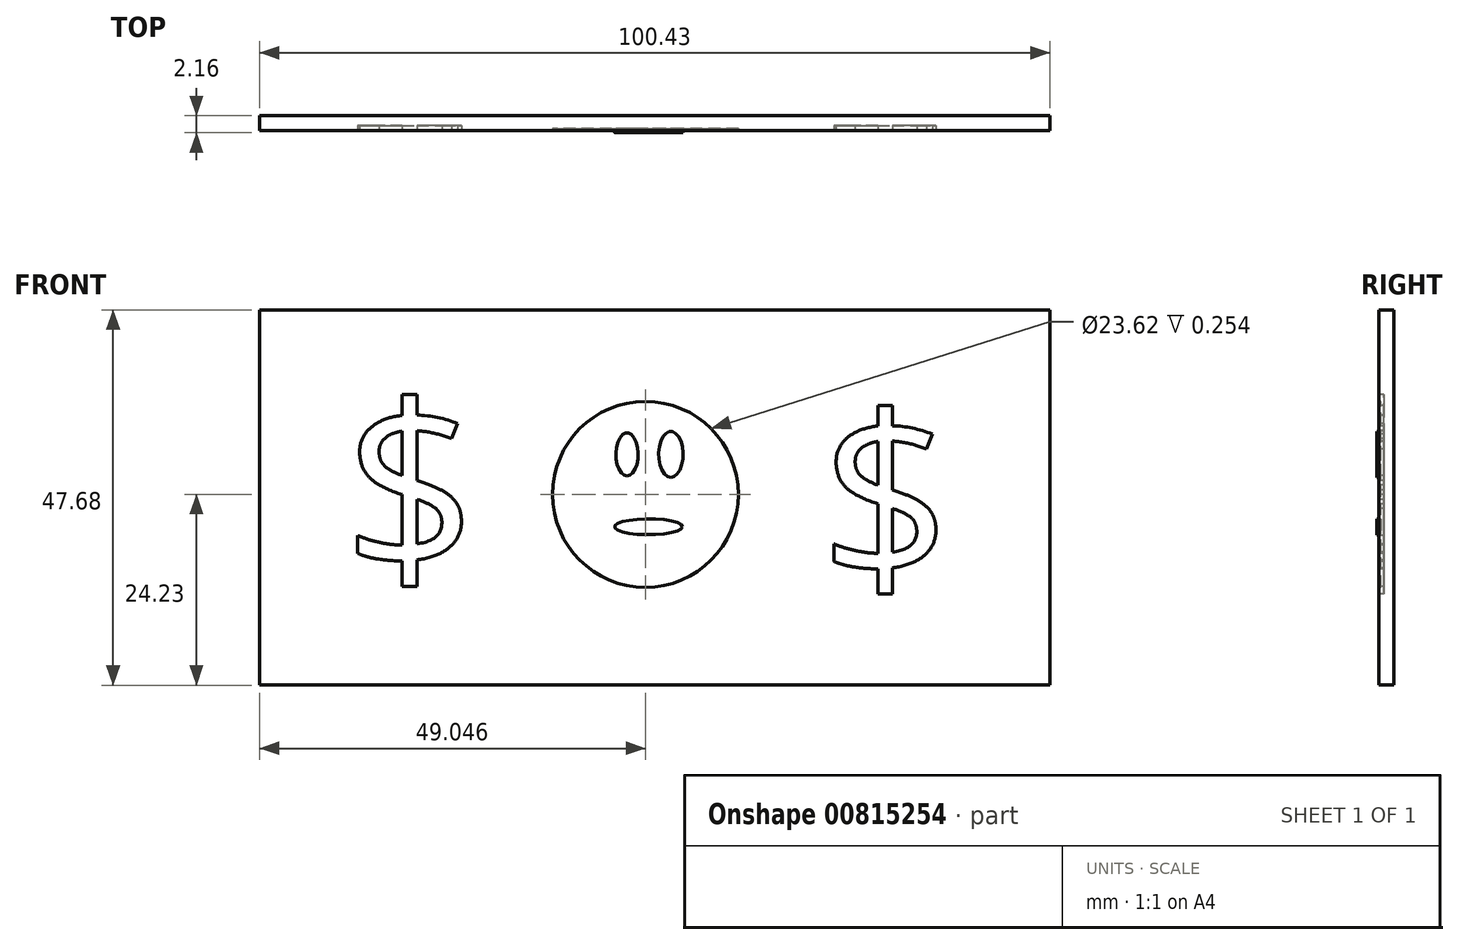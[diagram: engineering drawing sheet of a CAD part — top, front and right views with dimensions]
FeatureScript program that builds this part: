
annotation { "Feature Type Name" : "Feature", "Feature Type Description" : "" }
export const myFeature = defineFeature(function(context is Context, id is Id, definition is map)
    precondition{}
    {
        {
            var Q0;
            Q0=qCreatedBy(makeId("Front.planeOp"),FACE);
            var sketch = newSketch(context, id + "F0", { "sketchPlane" : qUnion([Q0])});
            skLineSegment(sketch, "E0.bottom", {"start": v(-52.27, 23.45) * mm, "end": v(48.16, 23.45) * mm});
            skLineSegment(sketch, "E0.top", {"start": v(-52.27, -24.23) * mm, "end": v(48.16, -24.23) * mm});
            skLineSegment(sketch, "E0.left", {"start": v(-52.27, 23.45) * mm, "end": v(-52.27, -24.23) * mm});
            skLineSegment(sketch, "E0.right", {"start": v(48.16, 23.45) * mm, "end": v(48.16, -24.23) * mm});
            skSolve(sketch);
        }
        {
            var Q0;
            Q0=makeQuery(id+"F0.imprint","IMPRINT",FACE,{"disambiguationData":[TD([[makeQuery(id+"F0.imprint","IMPRINT",EDGE,{"derivedFrom":sQuery(id+"F0.wireOp",EDGE,"E0.bottom")}),-1.0]])]});
            extrude(context, id + "F1", {"entities" : qUnion([Q0]), "depth" : 1.9 * mm, "offsetDistance" : 25.4 * mm});
        }
        {
            var Q0;
            Q0=makeQuery(id+"F1.opExtrude","CAP_FACE",FACE,{"disambiguationData":[OSD([sQuery(id+"F0.wireOp",EDGE,"E0.bottom"),sQuery(id+"F0.wireOp",EDGE,"E0.top"),sQuery(id+"F0.wireOp",EDGE,"E0.left"),sQuery(id+"F0.wireOp",EDGE,"E0.right")])],"isStart":false});
            var sketch = newSketch(context, id + "F2", { "sketchPlane" : qUnion([Q0])});
            skText(sketch, "E1", { "text": "$", "fontName": "OpenSans-Regular.ttf"});
            const initialGuessF2  = {"E1": [-0.04171, -0.00996, 1, 0, 0.0215]};
            skSetInitialGuess(sketch, initialGuessF2);
            skSolve(sketch);
        }
        {
            var Q0;
            Q0=makeQuery(id+"F2.imprint","IMPRINT",FACE,{"disambiguationData":[TD([[makeQuery(id+"F2.imprint","IMPRINT",EDGE,{"derivedFrom":sQuery(id+"F2.wireOp",EDGE,"E1.sketch_text.stroke-0")}),1.0]])]});
            var sketch = newSketch(context, id + "F3", { "sketchPlane" : qUnion([Q0])});
            skText(sketch, "E2", { "text": "$", "fontName": "OpenSans-Regular.ttf"});
            const initialGuessF3  = {"E2": [0.01885, -0.01094, 1, 0, 0.0211]};
            skSetInitialGuess(sketch, initialGuessF3);
            skSolve(sketch);
        }
        {
            var Q0;
            Q0 = qSketchRegion(id + "F2", true);
            var Q1;
            Q1 = qSketchRegion(id + "F3", true);
            extrude(context, id + "F4", {"entities" : qUnion([Q0, Q1]), "operationType" : NewBodyOperationType.REMOVE, "oppositeDirection" : true, "depth" : 0.64 * mm, "offsetDistance" : 25.4 * mm});
        }
        {
            var Q0;
            {var subQ0=sQuery(id+"F0.wireOp",EDGE,"E0.right");var subQ1=sQuery(id+"F0.wireOp",EDGE,"E0.left");var subQ2=sQuery(id+"F0.wireOp",EDGE,"E0.bottom");var subQ3=sQuery(id+"F0.wireOp",EDGE,"E0.top");Q0=makeQuery(id+"F4.boolean.opBoolean","SPLIT",FACE,{"disambiguationData":[TD([makeQuery(id+"F1.opExtrude","SWEPT_FACE",FACE,{"disambiguationData":[OSD([subQ2])]})])],"derivedFrom":makeQuery(id+"F1.opExtrude","CAP_FACE",FACE,{"disambiguationData":[OSD([subQ2,subQ3,subQ1,subQ0])],"isStart":false})});}
            var sketch = newSketch(context, id + "F5", { "sketchPlane" : qUnion([Q0])});
            skCircle(sketch, "E3", {"center": v(-3.22, 0) * mm, "radius": 11.8 * mm});
            skSolve(sketch);
        }
        {
            var Q0;
            Q0=makeQuery(id+"F5.imprint","IMPRINT",FACE,{"disambiguationData":[TD([[makeQuery(id+"F5.imprint","IMPRINT",EDGE,{"derivedFrom":sQuery(id+"F5.wireOp",EDGE,"E3")}),1.0]])]});
            extrude(context, id + "F6", {"entities" : qUnion([Q0]), "operationType" : NewBodyOperationType.REMOVE, "oppositeDirection" : true, "depth" : 0.25 * mm, "offsetDistance" : 25.4 * mm});
        }
        {
            var Q0;
            Q0=makeQuery(id+"F6.boolean.opBoolean","COPY",FACE,{"derivedFrom":makeQuery(id+"F6.opExtrude","CAP_FACE",FACE,{"disambiguationData":[OSD([sQuery(id+"F5.wireOp",EDGE,"E3")])],"isStart":false})});
            var sketch = newSketch(context, id + "F7", { "sketchPlane" : qUnion([Q0])});
            skEllipse(sketch, "E4", {"center": v(-5.57, 5.08) * mm, "majorRadius": 2.74 * mm, "minorRadius": 1.4 * mm, "majorAxis": v(0, -1)});
            skEllipse(sketch, "E5", {"center": v(0, 5.08) * mm, "majorRadius": 2.93 * mm, "minorRadius": 1.55 * mm, "majorAxis": v(0, -1)});
            skPoint(sketch, "E5.centerSnap0", {"position": v(-4.17, 5.08) * mm});
            skEllipse(sketch, "E6", {"center": v(-2.83, -4.1) * mm, "majorRadius": 4.3 * mm, "minorRadius": 1.01 * mm, "majorAxis": v(1, 0)});
            skSolve(sketch);
        }
        {
            var Q0;
            Q0=makeQuery(id+"F7.imprint","IMPRINT",FACE,{"disambiguationData":[TD([[makeQuery(id+"F7.imprint","IMPRINT",EDGE,{"derivedFrom":sQuery(id+"F7.wireOp",EDGE,"E4")}),1.0]])]});
            var Q1;
            Q1=makeQuery(id+"F7.imprint","IMPRINT",FACE,{"disambiguationData":[TD([[makeQuery(id+"F7.imprint","IMPRINT",EDGE,{"derivedFrom":sQuery(id+"F7.wireOp",EDGE,"E5")}),1.0]])]});
            var Q2;
            Q2=makeQuery(id+"F7.imprint","IMPRINT",FACE,{"disambiguationData":[TD([[makeQuery(id+"F7.imprint","IMPRINT",EDGE,{"derivedFrom":sQuery(id+"F7.wireOp",EDGE,"E6")}),1.0]])]});
            extrude(context, id + "F8", {"entities" : qUnion([Q0, Q1, Q2]), "operationType" : NewBodyOperationType.ADD, "depth" : 0.5 * mm, "offsetDistance" : 25.4 * mm});
        }
    });
